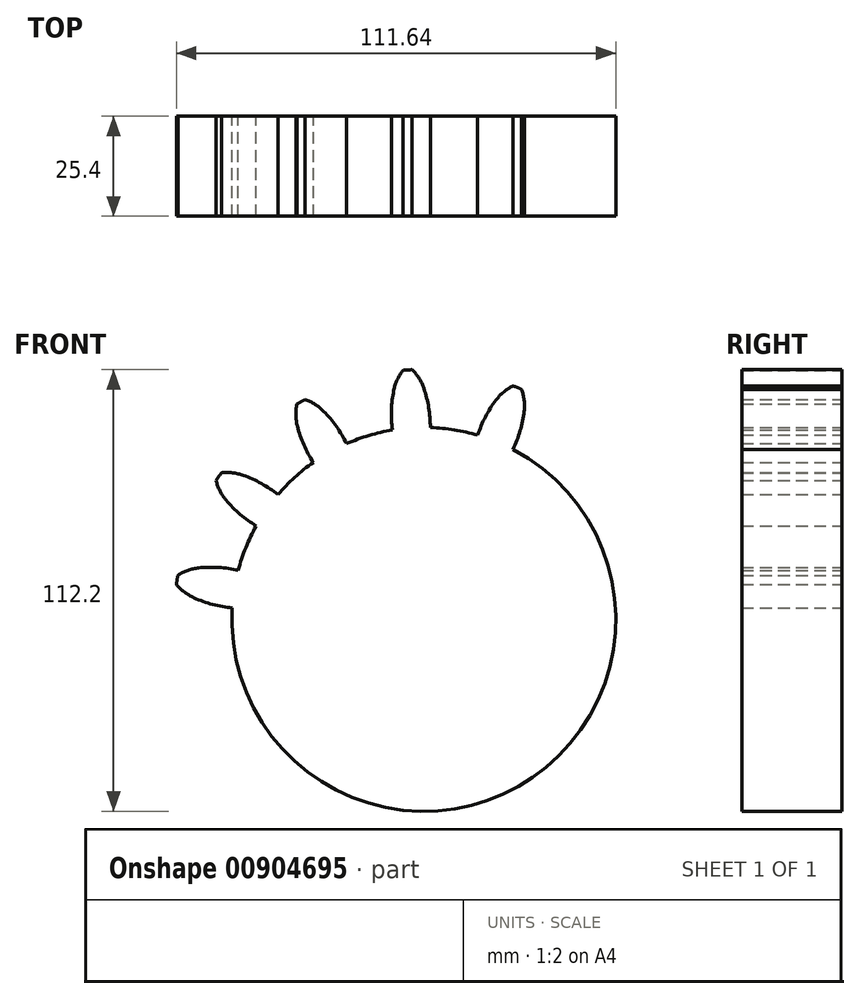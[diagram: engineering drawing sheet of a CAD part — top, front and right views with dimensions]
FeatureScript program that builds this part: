
annotation { "Feature Type Name" : "Feature", "Feature Type Description" : "" }
export const myFeature = defineFeature(function(context is Context, id is Id, definition is map)
    precondition{}
    {
        {
            var Q0;
            Q0=qCreatedBy(makeId("Front.planeOp"),FACE);
            var sketch = newSketch(context, id + "F0", { "sketchPlane" : qUnion([Q0])});
            skCircle(sketch, "E0", {"center": v(0, 0) * mm, "radius": 63.5 * mm, "construction": true});
            skCircle(sketch, "E1", {"center": v(0, 0) * mm, "radius": 58.67 * mm, "construction": true});
            skCircle(sketch, "E2", {"center": v(0, 0) * mm, "radius": 48.77 * mm});
            skLineSegment(sketch, "E3", {"start": v(0, 0) * mm, "end": v(0, 91) * mm, "construction": true});
            skLineSegment(sketch, "E4", {"start": v(0, 91) * mm, "end": v(0, 0) * mm, "construction": true});
            skLineSegment(sketch, "E5", {"start": v(0, 0) * mm, "end": v(-6, 91.66) * mm, "construction": true});
            skLineSegment(sketch, "E6", {"start": v(0, 58.67) * mm, "end": v(-74.22, 58.67) * mm, "construction": true});
            skLineSegment(sketch, "E7", {"start": v(0, 58.67) * mm, "end": v(-74.22, 31.66) * mm, "construction": true});
            skCircle(sketch, "E8", {"center": v(0, 0) * mm, "radius": 55.14 * mm, "construction": true});
            skCircle(sketch, "E9", {"center": v(0, 58.67) * mm, "radius": 14.6 * mm, "construction": true});
            skCircle(sketch, "E10", {"center": v(-13.63, 53.42) * mm, "radius": 14.6 * mm, "construction": true});
            skArc(sketch, "E11", {"start": v(0, 58.67) * mm, "mid": v(-1.22, 61.22) * mm, "end": v(-2.99, 63.43) * mm});
            skArc(sketch, "E12", {"start": v(1.64, 48.74) * mm, "mid": v(1.24, 53.78) * mm, "end": v(0, 58.67) * mm});
            skArc(sketch, "E13.MirrorCS", {"start": v(-7.98, 48.1) * mm, "mid": v(-8.25, 53.15) * mm, "end": v(-7.66, 58.17) * mm});
            skArc(sketch, "E14.MirrorCS", {"start": v(-7.66, 58.17) * mm, "mid": v(-6.78, 60.86) * mm, "end": v(-5.32, 63.28) * mm});
            skCircle(sketch, "E15.MirrorC", {"center": v(6.54, 54.75) * mm, "radius": 14.6 * mm, "construction": true});
            skArc(sketch, "E16", {"start": v(-2.99, 63.43) * mm, "mid": v(-4.15, 63.36) * mm, "end": v(-5.32, 63.28) * mm});
            skArc(sketch, "E17.1.0", {"start": v(-19.67, 44.62) * mm, "mid": v(-22.22, 48.99) * mm, "end": v(-25.46, 52.86) * mm});
            skArc(sketch, "E17.1.1", {"start": v(-28.07, 39.88) * mm, "mid": v(-30.5, 44.31) * mm, "end": v(-32.14, 49.09) * mm});
            skArc(sketch, "E17.1.2", {"start": v(-32.14, 49.09) * mm, "mid": v(-32.52, 51.9) * mm, "end": v(-32.24, 54.7) * mm});
            skArc(sketch, "E17.1.3", {"start": v(-25.46, 52.86) * mm, "mid": v(-27.66, 54.63) * mm, "end": v(-30.21, 55.85) * mm});
            skArc(sketch, "E17.1.4", {"start": v(-30.21, 55.85) * mm, "mid": v(-31.23, 55.29) * mm, "end": v(-32.24, 54.7) * mm});
            skArc(sketch, "E17.2.0", {"start": v(-37.09, 31.67) * mm, "mid": v(-41.27, 34.5) * mm, "end": v(-45.87, 36.58) * mm});
            skArc(sketch, "E17.2.1", {"start": v(-42.6, 23.75) * mm, "mid": v(-46.7, 26.7) * mm, "end": v(-50.26, 30.28) * mm});
            skArc(sketch, "E17.2.2", {"start": v(-50.26, 30.28) * mm, "mid": v(-51.81, 32.64) * mm, "end": v(-52.79, 35.3) * mm});
            skArc(sketch, "E17.2.3", {"start": v(-45.87, 36.58) * mm, "mid": v(-48.63, 37.22) * mm, "end": v(-51.46, 37.21) * mm});
            skArc(sketch, "E17.2.4", {"start": v(-51.46, 37.21) * mm, "mid": v(-52.13, 36.26) * mm, "end": v(-52.79, 35.3) * mm});
            skArc(sketch, "E17.3.0", {"start": v(-47.15, 12.44) * mm, "mid": v(-52.15, 13.17) * mm, "end": v(-57.2, 13.06) * mm});
            skArc(sketch, "E17.3.1", {"start": v(-48.68, 2.92) * mm, "mid": v(-53.66, 3.79) * mm, "end": v(-58.42, 5.48) * mm});
            skArc(sketch, "E17.3.2", {"start": v(-58.42, 5.48) * mm, "mid": v(-60.84, 6.93) * mm, "end": v(-62.87, 8.9) * mm});
            skArc(sketch, "E17.3.3", {"start": v(-57.2, 13.06) * mm, "mid": v(-59.96, 12.43) * mm, "end": v(-62.5, 11.2) * mm});
            skArc(sketch, "E17.3.4", {"start": v(-62.5, 11.2) * mm, "mid": v(-62.7, 10.05) * mm, "end": v(-62.87, 8.9) * mm});
            skArc(sketch, "E17.4.0", {"start": v(-47.88, -9.25) * mm, "mid": v(-52.7, -10.76) * mm, "end": v(-57.2, -13.06) * mm});
            skArc(sketch, "E17.4.1", {"start": v(-45.13, -18.49) * mm, "mid": v(-49.99, -19.87) * mm, "end": v(-55, -20.41) * mm});
            skArc(sketch, "E17.4.2", {"start": v(-55, -20.41) * mm, "mid": v(-57.82, -20.15) * mm, "end": v(-60.5, -19.26) * mm});
            skArc(sketch, "E17.4.3", {"start": v(-57.2, -13.06) * mm, "mid": v(-59.42, -14.81) * mm, "end": v(-61.17, -17.03) * mm});
            skArc(sketch, "E17.4.4", {"start": v(-61.17, -17.03) * mm, "mid": v(-60.85, -18.15) * mm, "end": v(-60.5, -19.26) * mm});
            skArc(sketch, "E17.5.0", {"start": v(-39.13, -29.1) * mm, "mid": v(-42.81, -32.56) * mm, "end": v(-45.87, -36.58) * mm});
            skArc(sketch, "E17.5.1", {"start": v(-32.64, -36.24) * mm, "mid": v(-36.42, -39.59) * mm, "end": v(-40.7, -42.26) * mm});
            skArc(sketch, "E17.5.2", {"start": v(-40.7, -42.26) * mm, "mid": v(-43.35, -43.25) * mm, "end": v(-46.16, -43.6) * mm});
            skArc(sketch, "E17.5.3", {"start": v(-45.87, -36.58) * mm, "mid": v(-47.1, -39.13) * mm, "end": v(-47.73, -41.88) * mm});
            skArc(sketch, "E17.5.4", {"start": v(-47.73, -41.88) * mm, "mid": v(-46.95, -42.75) * mm, "end": v(-46.16, -43.6) * mm});
            skArc(sketch, "E17.6.0", {"start": v(-22.62, -43.2) * mm, "mid": v(-24.45, -47.91) * mm, "end": v(-25.46, -52.86) * mm});
            skArc(sketch, "E17.6.1", {"start": v(-13.68, -46.8) * mm, "mid": v(-15.63, -51.47) * mm, "end": v(-18.34, -55.73) * mm});
            skArc(sketch, "E17.6.2", {"start": v(-18.34, -55.73) * mm, "mid": v(-20.3, -57.78) * mm, "end": v(-22.67, -59.32) * mm});
            skArc(sketch, "E17.6.3", {"start": v(-25.46, -52.86) * mm, "mid": v(-25.46, -55.7) * mm, "end": v(-24.83, -58.45) * mm});
            skArc(sketch, "E17.6.4", {"start": v(-24.83, -58.45) * mm, "mid": v(-23.75, -58.9) * mm, "end": v(-22.67, -59.32) * mm});
            skArc(sketch, "E17.7.0", {"start": v(-1.64, -48.74) * mm, "mid": v(-1.24, -53.78) * mm, "end": v(0, -58.67) * mm});
            skArc(sketch, "E17.7.1", {"start": v(7.98, -48.1) * mm, "mid": v(8.25, -53.15) * mm, "end": v(7.66, -58.17) * mm});
            skArc(sketch, "E17.7.2", {"start": v(7.66, -58.17) * mm, "mid": v(6.78, -60.86) * mm, "end": v(5.32, -63.28) * mm});
            skArc(sketch, "E17.7.3", {"start": v(0, -58.67) * mm, "mid": v(1.22, -61.22) * mm, "end": v(2.99, -63.43) * mm});
            skArc(sketch, "E17.7.4", {"start": v(2.99, -63.43) * mm, "mid": v(4.15, -63.36) * mm, "end": v(5.32, -63.28) * mm});
            skArc(sketch, "E17.8.0", {"start": v(19.67, -44.62) * mm, "mid": v(22.22, -48.99) * mm, "end": v(25.46, -52.86) * mm});
            skArc(sketch, "E17.8.1", {"start": v(28.07, -39.88) * mm, "mid": v(30.5, -44.31) * mm, "end": v(32.14, -49.09) * mm});
            skArc(sketch, "E17.8.2", {"start": v(32.14, -49.09) * mm, "mid": v(32.52, -51.9) * mm, "end": v(32.24, -54.7) * mm});
            skArc(sketch, "E17.8.3", {"start": v(25.46, -52.86) * mm, "mid": v(27.66, -54.63) * mm, "end": v(30.21, -55.85) * mm});
            skArc(sketch, "E17.8.4", {"start": v(30.21, -55.85) * mm, "mid": v(31.23, -55.29) * mm, "end": v(32.24, -54.7) * mm});
            skArc(sketch, "E17.9.0", {"start": v(37.09, -31.67) * mm, "mid": v(41.27, -34.5) * mm, "end": v(45.87, -36.58) * mm});
            skArc(sketch, "E17.9.1", {"start": v(42.6, -23.75) * mm, "mid": v(46.7, -26.7) * mm, "end": v(50.26, -30.28) * mm});
            skArc(sketch, "E17.9.2", {"start": v(50.26, -30.28) * mm, "mid": v(51.81, -32.64) * mm, "end": v(52.79, -35.3) * mm});
            skArc(sketch, "E17.9.3", {"start": v(45.87, -36.58) * mm, "mid": v(48.63, -37.22) * mm, "end": v(51.46, -37.21) * mm});
            skArc(sketch, "E17.9.4", {"start": v(51.46, -37.21) * mm, "mid": v(52.13, -36.26) * mm, "end": v(52.79, -35.3) * mm});
            skArc(sketch, "E17.10.0", {"start": v(47.15, -12.44) * mm, "mid": v(52.15, -13.17) * mm, "end": v(57.2, -13.06) * mm});
            skArc(sketch, "E17.10.1", {"start": v(48.68, -2.92) * mm, "mid": v(53.66, -3.79) * mm, "end": v(58.42, -5.48) * mm});
            skArc(sketch, "E17.10.2", {"start": v(58.42, -5.48) * mm, "mid": v(60.84, -6.93) * mm, "end": v(62.87, -8.9) * mm});
            skArc(sketch, "E17.10.3", {"start": v(57.2, -13.06) * mm, "mid": v(59.96, -12.43) * mm, "end": v(62.5, -11.2) * mm});
            skArc(sketch, "E17.10.4", {"start": v(62.5, -11.2) * mm, "mid": v(62.7, -10.05) * mm, "end": v(62.87, -8.9) * mm});
            skArc(sketch, "E17.11.0", {"start": v(47.88, 9.25) * mm, "mid": v(52.7, 10.76) * mm, "end": v(57.2, 13.06) * mm});
            skArc(sketch, "E17.11.1", {"start": v(45.13, 18.49) * mm, "mid": v(49.99, 19.87) * mm, "end": v(55, 20.41) * mm});
            skArc(sketch, "E17.11.2", {"start": v(55, 20.41) * mm, "mid": v(57.82, 20.15) * mm, "end": v(60.5, 19.26) * mm});
            skArc(sketch, "E17.11.3", {"start": v(57.2, 13.06) * mm, "mid": v(59.42, 14.81) * mm, "end": v(61.17, 17.03) * mm});
            skArc(sketch, "E17.11.4", {"start": v(61.17, 17.03) * mm, "mid": v(60.85, 18.15) * mm, "end": v(60.5, 19.26) * mm});
            skArc(sketch, "E17.12.0", {"start": v(39.13, 29.1) * mm, "mid": v(42.81, 32.56) * mm, "end": v(45.87, 36.58) * mm});
            skArc(sketch, "E17.12.1", {"start": v(32.64, 36.24) * mm, "mid": v(36.42, 39.59) * mm, "end": v(40.7, 42.26) * mm});
            skArc(sketch, "E17.12.2", {"start": v(40.7, 42.26) * mm, "mid": v(43.35, 43.25) * mm, "end": v(46.16, 43.6) * mm});
            skArc(sketch, "E17.12.3", {"start": v(45.87, 36.58) * mm, "mid": v(47.1, 39.13) * mm, "end": v(47.73, 41.88) * mm});
            skArc(sketch, "E17.12.4", {"start": v(47.73, 41.88) * mm, "mid": v(46.95, 42.75) * mm, "end": v(46.16, 43.6) * mm});
            skArc(sketch, "E17.13.0", {"start": v(22.62, 43.2) * mm, "mid": v(24.45, 47.91) * mm, "end": v(25.46, 52.86) * mm});
            skArc(sketch, "E17.13.1", {"start": v(13.68, 46.8) * mm, "mid": v(15.63, 51.47) * mm, "end": v(18.34, 55.73) * mm});
            skArc(sketch, "E17.13.2", {"start": v(18.34, 55.73) * mm, "mid": v(20.3, 57.78) * mm, "end": v(22.67, 59.32) * mm});
            skArc(sketch, "E17.13.3", {"start": v(25.46, 52.86) * mm, "mid": v(25.46, 55.7) * mm, "end": v(24.83, 58.45) * mm});
            skArc(sketch, "E17.13.4", {"start": v(24.83, 58.45) * mm, "mid": v(23.75, 58.9) * mm, "end": v(22.67, 59.32) * mm});
            skSolve(sketch);
        }
        {
            var Q0;
            {var subQ0=sQuery(id+"F0.wireOp",EDGE,"E2");var subQ18=makeQuery(id+"F0.imprint","INTERSECT",VERTEX,{"derivedFrom":[subQ0,sQuery(id+"F0.wireOp",EDGE,"E17.7.1")]});Q0=makeQuery(id+"F0.imprint","IMPRINT",FACE,{"disambiguationData":[TD([[makeQuery(id+"F0.imprint","IMPRINT",EDGE,{"disambiguationData":[TD([[subQ18,-1.0]])],"derivedFrom":subQ0}),1.0]])]});}
            var Q1;
            {var subQ0=sQuery(id+"F0.wireOp",EDGE,"E17.3.0");Q1=makeQuery(id+"F0.imprint","IMPRINT",FACE,{"disambiguationData":[TD([[makeQuery(id+"F0.imprint","IMPRINT",EDGE,{"derivedFrom":subQ0}),1.0]])]});}
            var Q2;
            {var subQ1=sQuery(id+"F0.wireOp",EDGE,"E17.2.0");Q2=makeQuery(id+"F0.imprint","IMPRINT",FACE,{"disambiguationData":[TD([[makeQuery(id+"F0.imprint","IMPRINT",EDGE,{"derivedFrom":subQ1}),1.0]])]});}
            var Q3;
            {var subQ1=sQuery(id+"F0.wireOp",EDGE,"E17.1.0");Q3=makeQuery(id+"F0.imprint","IMPRINT",FACE,{"disambiguationData":[TD([[makeQuery(id+"F0.imprint","IMPRINT",EDGE,{"derivedFrom":subQ1}),1.0]])]});}
            var Q4;
            Q4=makeQuery(id+"F0.imprint","IMPRINT",FACE,{"disambiguationData":[TD([[makeQuery(id+"F0.imprint","IMPRINT",EDGE,{"derivedFrom":sQuery(id+"F0.wireOp",EDGE,"E11")}),1.0]])]});
            var Q5;
            {var subQ1=sQuery(id+"F0.wireOp",EDGE,"E17.13.0");Q5=makeQuery(id+"F0.imprint","IMPRINT",FACE,{"disambiguationData":[TD([[makeQuery(id+"F0.imprint","IMPRINT",EDGE,{"derivedFrom":subQ1}),1.0]])]});}
            extrude(context, id + "F1", {"entities" : qUnion([Q0, Q1, Q2, Q3, Q4, Q5]), "depth" : 25.4 * mm, "offsetDistance" : 25.4 * mm});
        }
    });
